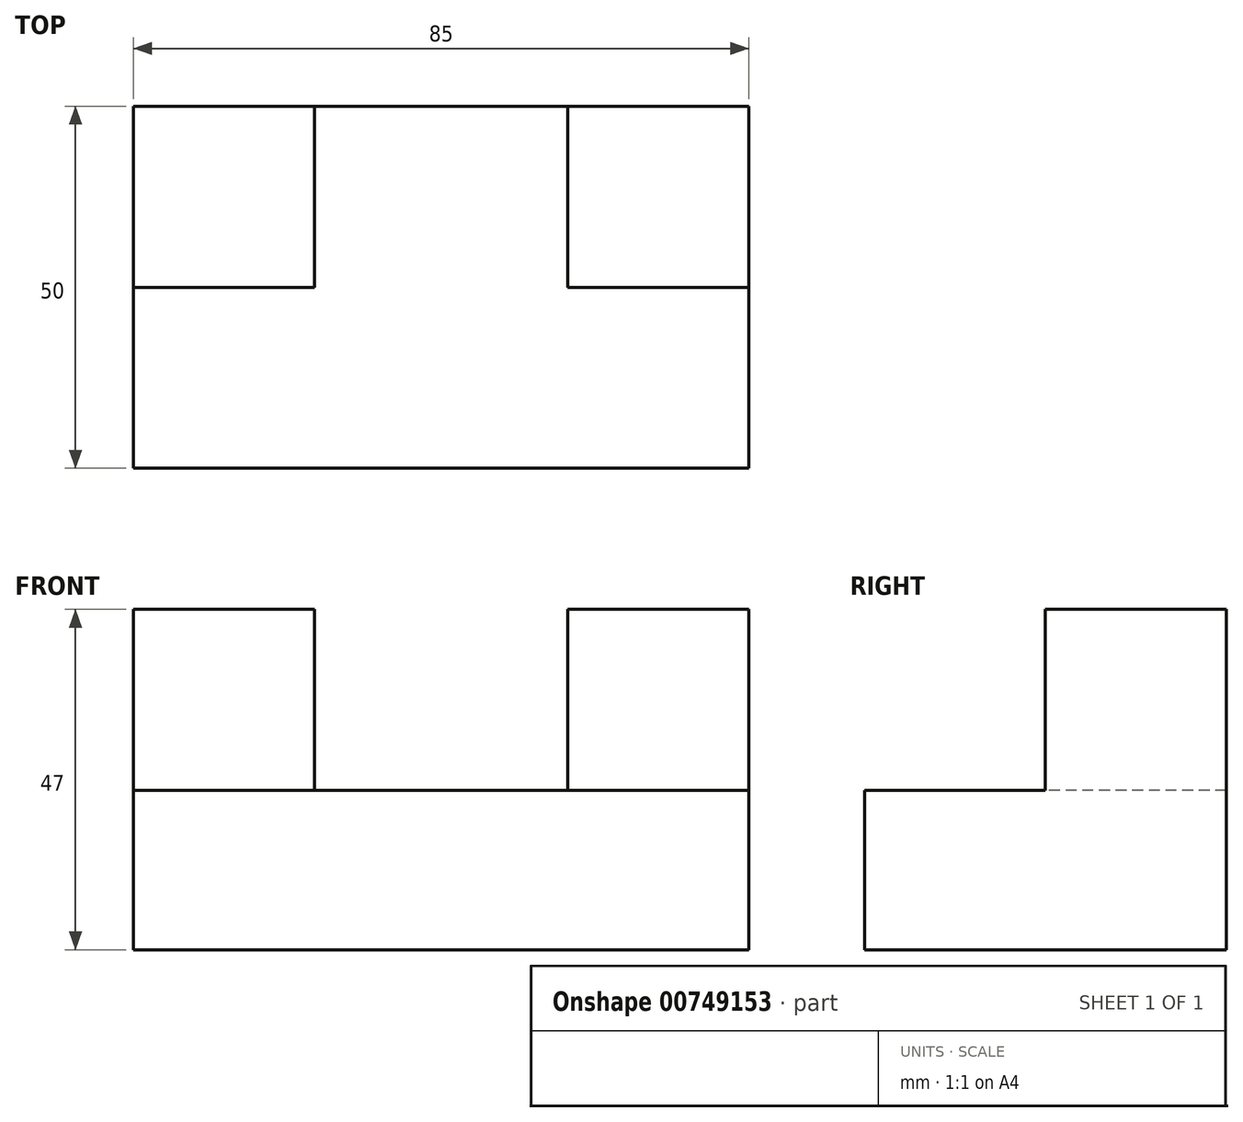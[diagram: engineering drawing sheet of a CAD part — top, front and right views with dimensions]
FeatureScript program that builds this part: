
annotation { "Feature Type Name" : "Feature", "Feature Type Description" : "" }
export const myFeature = defineFeature(function(context is Context, id is Id, definition is map)
    precondition{}
    {
        {
            var Q0;
            Q0=qCreatedBy(makeId("Front.planeOp"),FACE);
            var sketch = newSketch(context, id + "F0", { "sketchPlane" : qUnion([Q0])});
            skLineSegment(sketch, "E0.bottom", {"start": v(-42.5, -11) * mm, "end": v(42.5, -11) * mm});
            skLineSegment(sketch, "E0.top", {"start": v(-42.5, 11) * mm, "end": v(42.5, 11) * mm});
            skLineSegment(sketch, "E0.left", {"start": v(-42.5, -11) * mm, "end": v(-42.5, 11) * mm});
            skLineSegment(sketch, "E0.right", {"start": v(42.5, -11) * mm, "end": v(42.5, 11) * mm});
            skPoint(sketch, "E0.middle", {"position": v(0, 0) * mm});
            skSolve(sketch);
        }
        {
            var Q0;
            Q0=makeQuery(id+"F0.imprint","IMPRINT",FACE,{"disambiguationData":[TD([[makeQuery(id+"F0.imprint","IMPRINT",EDGE,{"derivedFrom":sQuery(id+"F0.wireOp",EDGE,"E0.bottom")}),1.0]])]});
            extrude(context, id + "F1", {"entities" : qUnion([Q0]), "depth" : 50 * mm, "offsetDistance" : 25 * mm});
        }
        {
            var Q0;
            Q0=makeQuery(id+"F1.opExtrude","SWEPT_FACE",FACE,{"disambiguationData":[OSD([sQuery(id+"F0.wireOp",EDGE,"E0.top")])]});
            var sketch = newSketch(context, id + "F2", { "sketchPlane" : qUnion([Q0])});
            skLineSegment(sketch, "E1.bottom", {"start": v(-42.5, 0) * mm, "end": v(-17.5, 0) * mm});
            skLineSegment(sketch, "E1.top", {"start": v(-42.5, -25) * mm, "end": v(-17.5, -25) * mm});
            skLineSegment(sketch, "E1.left", {"start": v(-42.5, 0) * mm, "end": v(-42.5, -25) * mm});
            skLineSegment(sketch, "E1.right", {"start": v(-17.5, 0) * mm, "end": v(-17.5, -25) * mm});
            skLineSegment(sketch, "E2.bottom", {"start": v(42.5, 0) * mm, "end": v(17.5, 0) * mm});
            skLineSegment(sketch, "E2.top", {"start": v(42.5, -25) * mm, "end": v(17.5, -25) * mm});
            skLineSegment(sketch, "E2.left", {"start": v(42.5, 0) * mm, "end": v(42.5, -25) * mm});
            skLineSegment(sketch, "E2.right", {"start": v(17.5, 0) * mm, "end": v(17.5, -25) * mm});
            skSolve(sketch);
        }
        {
            var Q0;
            Q0=makeQuery(id+"F2.imprint","IMPRINT",FACE,{"disambiguationData":[TD([[makeQuery(id+"F2.imprint","IMPRINT",EDGE,{"derivedFrom":sQuery(id+"F2.wireOp",EDGE,"E2.bottom")}),-1.0]])]});
            extrude(context, id + "F3", {"entities" : qUnion([Q0]), "operationType" : NewBodyOperationType.ADD, "depth" : 25 * mm, "offsetDistance" : 25 * mm});
        }
        {
            var Q0;
            Q0=makeQuery(id+"F1.opExtrude","SWEPT_FACE",FACE,{"disambiguationData":[OSD([sQuery(id+"F0.wireOp",EDGE,"E0.top")])]});
            var sketch = newSketch(context, id + "F4", { "sketchPlane" : qUnion([Q0])});
            skLineSegment(sketch, "E3.bottom", {"start": v(-42.5, 0) * mm, "end": v(-17.5, 0) * mm});
            skLineSegment(sketch, "E3.top", {"start": v(-42.5, -25) * mm, "end": v(-17.5, -25) * mm});
            skLineSegment(sketch, "E3.left", {"start": v(-42.5, 0) * mm, "end": v(-42.5, -25) * mm});
            skLineSegment(sketch, "E3.right", {"start": v(-17.5, 0) * mm, "end": v(-17.5, -25) * mm});
            skSolve(sketch);
        }
        {
            var Q0;
            Q0=makeQuery(id+"F4.imprint","IMPRINT",FACE,{"disambiguationData":[TD([[makeQuery(id+"F4.imprint","IMPRINT",EDGE,{"derivedFrom":sQuery(id+"F4.wireOp",EDGE,"E3.bottom")}),-1.0]])]});
            extrude(context, id + "F5", {"entities" : qUnion([Q0]), "operationType" : NewBodyOperationType.ADD, "depth" : 25 * mm, "offsetDistance" : 25 * mm});
        }
    });
